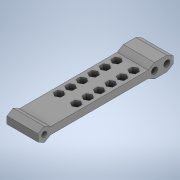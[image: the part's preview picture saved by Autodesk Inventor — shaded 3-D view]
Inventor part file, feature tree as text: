
AUTODESK INVENTOR PART (.ipt)
format: ipt  version: 2020 (Build 240168000, 168)  size: 385,024 bytes
history: native  units: in
note: dims shown in document units (in); Inventor stores cm internally (conversion verified against a paired STEP export)
features: sketch x6, extrude x5, projected_geometry x3, plane x2, mirror x1
ambient origin geometry x8: Origin, YZ Plane, XZ Plane, XY Plane, X Axis, Y Axis, Z Axis, Center Point
bodies: Solid1 (feature_tree)
feature tree (17):
  extrude  "Extrusion1"  Depth=3.4256in
  plane  "Work Plane1"
  extrude  "Extrusion2"  Depth=0.7874in
  sketch  "Sketch4"  dims[d4=0.0in d5=0.0827in]
  extrude  "Extrusion4"  Depth=0.0827in
  plane  "Work Plane2"
  extrude  "Extrusion6"  Depth=3.1106in
  mirror  "Mirror2"
  extrude  "Extrusion7"  Depth=0.315in
  sketch  "Sketch1"  dims[d0=0.1818in d1=3.4256in]
  sketch  "Sketch2"  dims[d2=0.1299in d3=0.7874in]
  sketch  "Sketch5"  dims[d6=0.7874in d7=0.0in d28=3.1106in]
  sketch  "Sketch7"  dims[d29=0.315in d31=0.315in]
  projected_geometry  "Projected Loop7"
  projected_geometry  "Projected Loop8"
  sketch  "Sketch8"  dims[d33=0.1575in d34=0.2362in d35=0.0in d38=0.315in d39=0.2756in d40=-0.3092in d41=0.0787in d42=0.0787in d43=0.0787in d44=2.3622in d46=0.2913in d47=0.3937in d49=0.3937in d51=2.3622in d53=0.2913in d54=0.3937in d56=0.3937in d58=0.0in d59=0.0in]
  projected_geometry  "Projected Loop9"
